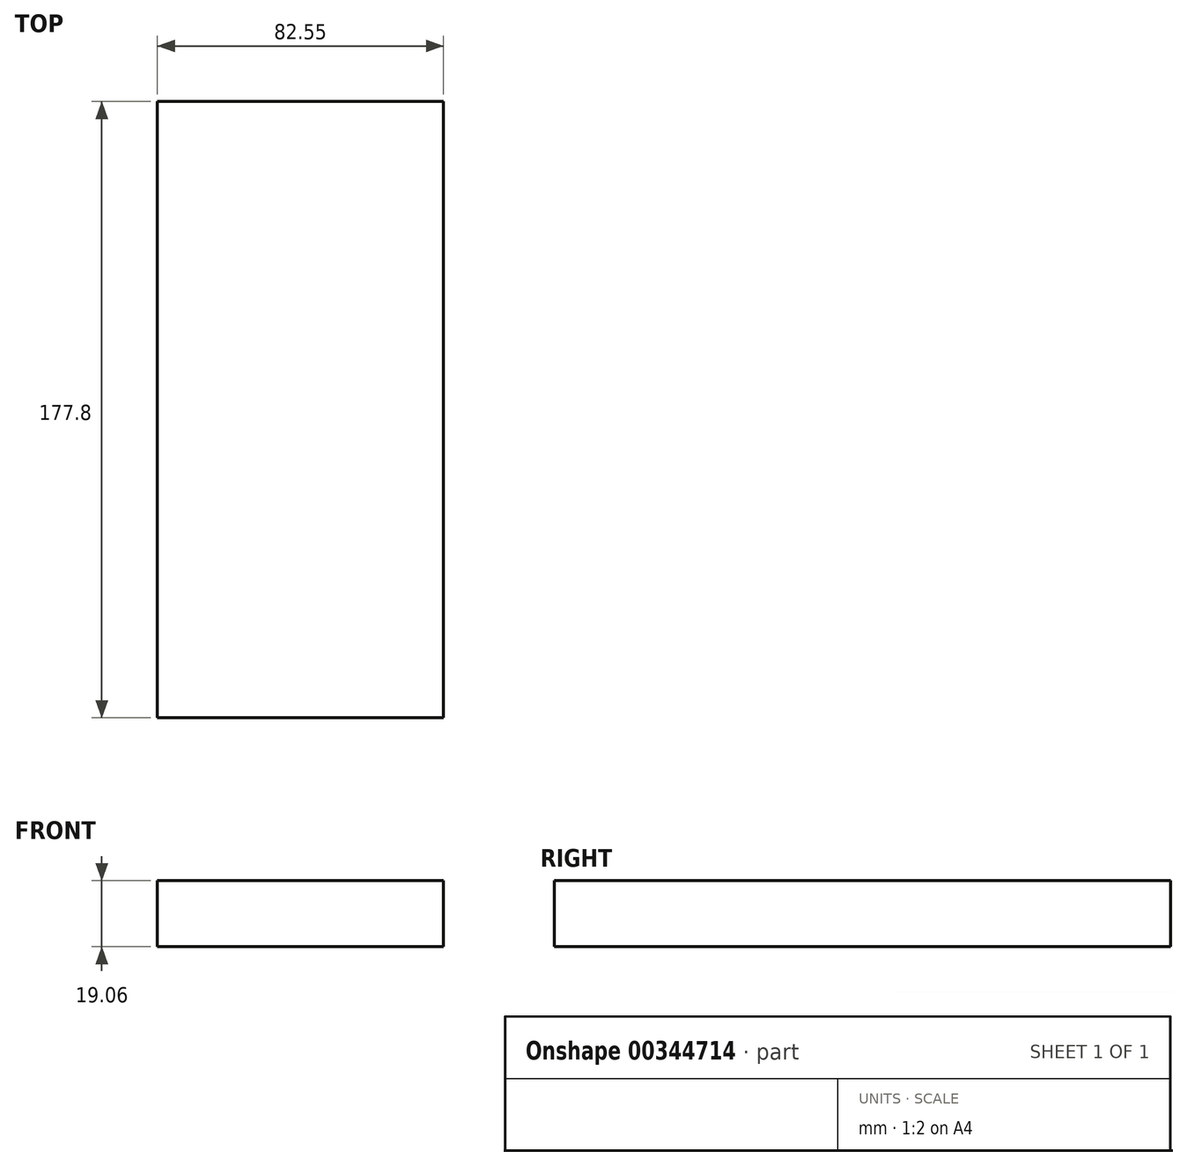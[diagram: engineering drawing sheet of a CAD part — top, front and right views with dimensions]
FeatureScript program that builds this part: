
annotation { "Feature Type Name" : "Feature", "Feature Type Description" : "" }
export const myFeature = defineFeature(function(context is Context, id is Id, definition is map)
    precondition{}
    {
        {
            var Q0;
            Q0=qCreatedBy(makeId("Front.planeOp"),FACE);
            var sketch = newSketch(context, id + "F0", { "sketchPlane" : qUnion([Q0])});
            skLineSegment(sketch, "E0.bottom", {"start": v(41.27, 9.53) * mm, "end": v(-41.28, 9.53) * mm});
            skLineSegment(sketch, "E0.top", {"start": v(41.28, -9.52) * mm, "end": v(-41.27, -9.52) * mm});
            skLineSegment(sketch, "E0.left", {"start": v(41.28, 9.53) * mm, "end": v(41.28, -9.52) * mm});
            skLineSegment(sketch, "E0.right", {"start": v(-41.28, 9.53) * mm, "end": v(-41.27, -9.52) * mm});
            skPoint(sketch, "E0.middle", {"position": v(0, 0) * mm});
            skLineSegment(sketch, "E1.bottom", {"start": v(60.32, 38.1) * mm, "end": v(111.12, 38.1) * mm});
            skLineSegment(sketch, "E1.top", {"start": v(60.32, 66.68) * mm, "end": v(111.12, 66.68) * mm});
            skLineSegment(sketch, "E1.left", {"start": v(60.32, 38.1) * mm, "end": v(60.32, 66.68) * mm});
            skLineSegment(sketch, "E1.right", {"start": v(111.12, 38.1) * mm, "end": v(111.12, 66.68) * mm});
            skPoint(sketch, "E1.middle", {"position": v(85.72, 52.39) * mm});
            skLineSegment(sketch, "E2", {"start": v(41.27, 9.53) * mm, "end": v(41.27, 27) * mm});
            skArc(sketch, "E3", {"start": v(41.27, 27) * mm, "mid": v(45.92, 38.23) * mm, "end": v(57.15, 42.88) * mm});
            skLineSegment(sketch, "E4", {"start": v(57.15, 42.88) * mm, "end": v(90.6, 42.88) * mm});
            skLineSegment(sketch, "E5.0", {"start": v(57.15, 61.93) * mm, "end": v(90.6, 61.93) * mm});
            skArc(sketch, "E5.1", {"start": v(22.23, 27) * mm, "mid": v(32.45, 51.7) * mm, "end": v(57.15, 61.93) * mm});
            skLineSegment(sketch, "E5.2", {"start": v(22.23, 9.53) * mm, "end": v(22.23, 27) * mm});
            skFitSpline(sketch, "E6", {"points": [v(-41.28, 9.53) * mm, v(57.15, 61.93) * mm], "startDerivative": vector(0.26, 105.64) * mm, "endDerivative": vector(268.53, 5.71) * mm});
            skSolve(sketch);
        }
        {
            var Q0;
            Q0=makeQuery(id+"F0.imprint","IMPRINT",FACE,{"disambiguationData":[TD([[makeQuery(id+"F0.imprint","IMPRINT",EDGE,{"derivedFrom":sQuery(id+"F0.wireOp",EDGE,"E0.top")}),-1.0]])]});
            extrude(context, id + "F1", {"entities" : qUnion([Q0]), "endBound" : BoundingType.SYMMETRIC, "depth" : 177.8 * mm, "offsetDistance" : 25.4 * mm});
        }
    });
